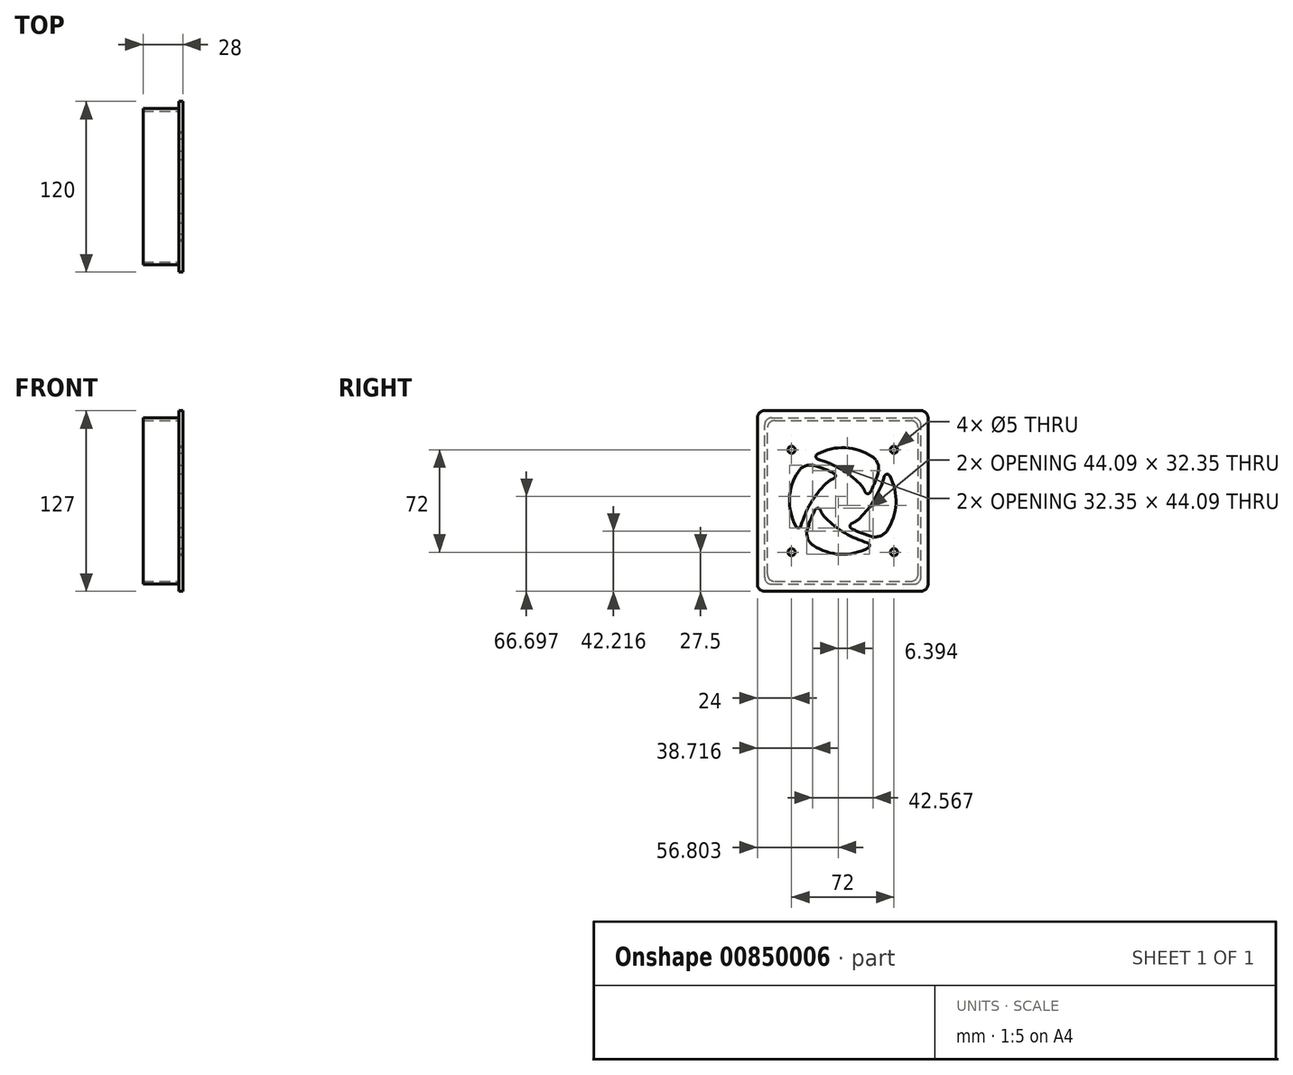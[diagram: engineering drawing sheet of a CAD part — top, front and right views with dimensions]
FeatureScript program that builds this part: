
annotation { "Feature Type Name" : "Feature", "Feature Type Description" : "" }
export const myFeature = defineFeature(function(context is Context, id is Id, definition is map)
    precondition{}
    {
        {
            var Q0;
            Q0=qCreatedBy(makeId("Right.planeOp"),FACE);
            var sketch = newSketch(context, id + "F0", { "sketchPlane" : qUnion([Q0])});
            skLineSegment(sketch, "E0.bottom", {"start": v(60, 63.5) * mm, "end": v(-60, 63.5) * mm});
            skLineSegment(sketch, "E0.top", {"start": v(60, -63.5) * mm, "end": v(-60, -63.5) * mm});
            skLineSegment(sketch, "E0.left", {"start": v(60, 63.5) * mm, "end": v(60, -63.5) * mm});
            skLineSegment(sketch, "E0.right", {"start": v(-60, 63.5) * mm, "end": v(-60, -63.5) * mm});
            skPoint(sketch, "E0.middle", {"position": v(0, 0) * mm});
            skSolve(sketch);
        }
        {
            var Q0;
            Q0 = qSketchRegion(id + "F0", true);
            extrude(context, id + "F1", {"entities" : qUnion([Q0]), "depth" : 3 * mm, "offsetDistance" : 25 * mm});
        }
        {
            var Q0;
            Q0=makeQuery(id+"F1.opExtrude","SWEPT_EDGE",EDGE,{"disambiguationData":[OSD([sQuery(id+"F0.wireOp",EDGE,"E0.bottom"),sQuery(id+"F0.wireOp",EDGE,"E0.right")])]});
            var Q1;
            Q1=makeQuery(id+"F1.opExtrude","SWEPT_EDGE",EDGE,{"disambiguationData":[OSD([sQuery(id+"F0.wireOp",EDGE,"E0.bottom"),sQuery(id+"F0.wireOp",EDGE,"E0.left")])]});
            var Q2;
            Q2=makeQuery(id+"F1.opExtrude","SWEPT_EDGE",EDGE,{"disambiguationData":[OSD([sQuery(id+"F0.wireOp",EDGE,"E0.top"),sQuery(id+"F0.wireOp",EDGE,"E0.left")])]});
            var Q3;
            Q3=makeQuery(id+"F1.opExtrude","SWEPT_EDGE",EDGE,{"disambiguationData":[OSD([sQuery(id+"F0.wireOp",EDGE,"E0.top"),sQuery(id+"F0.wireOp",EDGE,"E0.right")])]});
            fillet(context, id + "F2", {"entities" : qUnion([Q0, Q1, Q2, Q3]), "radius" : 5 * mm, "tangentPropagation" : true, "allowEdgeOverflow" : false});
        }
        {
            var Q0;
            Q0=makeQuery(id+"F1.opExtrude","CAP_FACE",FACE,{"disambiguationData":[OSD([sQuery(id+"F0.wireOp",EDGE,"E0.bottom"),sQuery(id+"F0.wireOp",EDGE,"E0.top"),sQuery(id+"F0.wireOp",EDGE,"E0.left"),sQuery(id+"F0.wireOp",EDGE,"E0.right")])],"isStart":true});
            var sketch = newSketch(context, id + "F3", { "sketchPlane" : qUnion([Q0])});
            skLineSegment(sketch, "E1.bottom", {"start": v(50, -58.5) * mm, "end": v(-50, -58.5) * mm});
            skLineSegment(sketch, "E1.top", {"start": v(50, 58.5) * mm, "end": v(-50, 58.5) * mm});
            skLineSegment(sketch, "E1.left", {"start": v(55, -53.5) * mm, "end": v(55, 53.5) * mm});
            skLineSegment(sketch, "E1.right", {"start": v(-55, -53.5) * mm, "end": v(-55, 53.5) * mm});
            skPoint(sketch, "E1.middle", {"position": v(0, 0) * mm});
            skLineSegment(sketch, "E2.0", {"start": v(53, -51.5) * mm, "end": v(53, 51.5) * mm});
            skLineSegment(sketch, "E2.1", {"start": v(48, -56.5) * mm, "end": v(-48, -56.5) * mm});
            skLineSegment(sketch, "E2.2", {"start": v(-53, -51.5) * mm, "end": v(-53, 51.5) * mm});
            skLineSegment(sketch, "E2.3", {"start": v(48, 56.5) * mm, "end": v(-48, 56.5) * mm});
            skPoint(sketch, "E3.visualSharp", {"position": v(53, 56.5) * mm});
            skArc(sketch, "E3.filletArc", {"start": v(53, 51.5) * mm, "mid": v(51.54, 55.04) * mm, "end": v(48, 56.5) * mm});
            skPoint(sketch, "E4.visualSharp", {"position": v(55, 58.5) * mm});
            skArc(sketch, "E4.filletArc", {"start": v(55, 53.5) * mm, "mid": v(53.54, 57.04) * mm, "end": v(50, 58.5) * mm});
            skPoint(sketch, "E5.visualSharp", {"position": v(53, -56.5) * mm});
            skArc(sketch, "E5.filletArc", {"start": v(48, -56.5) * mm, "mid": v(51.54, -55.04) * mm, "end": v(53, -51.5) * mm});
            skPoint(sketch, "E6.visualSharp", {"position": v(55, -58.5) * mm});
            skArc(sketch, "E6.filletArc", {"start": v(50, -58.5) * mm, "mid": v(53.54, -57.04) * mm, "end": v(55, -53.5) * mm});
            skPoint(sketch, "E7.visualSharp", {"position": v(-53, 56.5) * mm});
            skArc(sketch, "E7.filletArc", {"start": v(-48, 56.5) * mm, "mid": v(-51.54, 55.04) * mm, "end": v(-53, 51.5) * mm});
            skPoint(sketch, "E8.visualSharp", {"position": v(-55, 58.5) * mm});
            skArc(sketch, "E8.filletArc", {"start": v(-50, 58.5) * mm, "mid": v(-53.54, 57.04) * mm, "end": v(-55, 53.5) * mm});
            skPoint(sketch, "E9.visualSharp", {"position": v(-53, -56.5) * mm});
            skArc(sketch, "E9.filletArc", {"start": v(-53, -51.5) * mm, "mid": v(-51.54, -55.04) * mm, "end": v(-48, -56.5) * mm});
            skPoint(sketch, "E10.visualSharp", {"position": v(-55, -58.5) * mm});
            skArc(sketch, "E10.filletArc", {"start": v(-55, -53.5) * mm, "mid": v(-53.54, -57.04) * mm, "end": v(-50, -58.5) * mm});
            skSolve(sketch);
        }
        {
            var Q0;
            Q0 = qSketchRegion(id + "F3", true);
            extrude(context, id + "F4", {"entities" : qUnion([Q0]), "operationType" : NewBodyOperationType.ADD, "depth" : 25 * mm, "offsetDistance" : 25 * mm});
        }
        {
            var Q0;
            Q0=makeQuery(id+"F4.boolean.opBoolean","SPLIT",FACE,{"disambiguationData":[TD([makeQuery(id+"F4.opExtrude","SWEPT_FACE",FACE,{"disambiguationData":[OSD([sQuery(id+"F3.wireOp",EDGE,"E2.0")])]})])],"derivedFrom":makeQuery(id+"F1.opExtrude","CAP_FACE",FACE,{"disambiguationData":[OSD([sQuery(id+"F0.wireOp",EDGE,"E0.bottom"),sQuery(id+"F0.wireOp",EDGE,"E0.top"),sQuery(id+"F0.wireOp",EDGE,"E0.left"),sQuery(id+"F0.wireOp",EDGE,"E0.right")])],"isStart":true})});
            var sketch = newSketch(context, id + "F5", { "sketchPlane" : qUnion([Q0])});
            skCircle(sketch, "E11", {"center": v(36, 36) * mm, "radius": 2.5 * mm});
            skCircle(sketch, "E12.0.1.0", {"center": v(36, -36) * mm, "radius": 2.5 * mm});
            skCircle(sketch, "E12.1.0.0", {"center": v(-36, 36) * mm, "radius": 2.5 * mm});
            skCircle(sketch, "E12.1.1.0", {"center": v(-36, -36) * mm, "radius": 2.5 * mm});
            skCircle(sketch, "E12.2.0.0", {"center": v(-108, 36) * mm, "radius": 2.5 * mm});
            skCircle(sketch, "E12.2.1.0", {"center": v(-108, -36) * mm, "radius": 2.5 * mm});
            skLineSegment(sketch, "E12.direction1", {"start": v(36, 36) * mm, "end": v(-36, 36) * mm, "construction": true});
            skLineSegment(sketch, "E12.direction2", {"start": v(36, 36) * mm, "end": v(36, -36) * mm, "construction": true});
            skSolve(sketch);
        }
        {
            var Q0;
            Q0 = qSketchRegion(id + "F5", true);
            extrude(context, id + "F6", {"entities" : qUnion([Q0]), "operationType" : NewBodyOperationType.REMOVE, "endBound" : BoundingType.THROUGH_ALL, "oppositeDirection" : true, "depth" : 25 * mm, "offsetDistance" : 25 * mm});
        }
        {
            var Q0;
            Q0=makeQuery(id+"F4.boolean.opBoolean","SPLIT",FACE,{"disambiguationData":[TD([makeQuery(id+"F4.opExtrude","SWEPT_FACE",FACE,{"disambiguationData":[OSD([sQuery(id+"F3.wireOp",EDGE,"E2.0")])]})])],"derivedFrom":makeQuery(id+"F1.opExtrude","CAP_FACE",FACE,{"disambiguationData":[OSD([sQuery(id+"F0.wireOp",EDGE,"E0.bottom"),sQuery(id+"F0.wireOp",EDGE,"E0.top"),sQuery(id+"F0.wireOp",EDGE,"E0.left"),sQuery(id+"F0.wireOp",EDGE,"E0.right")])],"isStart":true})});
            var sketch = newSketch(context, id + "F7", { "sketchPlane" : qUnion([Q0])});
            skArc(sketch, "E13", {"start": v(12.02, 12.02) * mm, "mid": v(7.39, 15.3) * mm, "end": v(1.93, 16.89) * mm});
            skArc(sketch, "E14", {"start": v(30.43, -21.9) * mm, "mid": v(37.4, 2.83) * mm, "end": v(26.8, 26.23) * mm});
            skArc(sketch, "E15", {"start": v(30.43, -21.9) * mm, "mid": v(23.69, -3.6) * mm, "end": v(12.02, 12.02) * mm});
            skArc(sketch, "E16.0", {"start": v(26.23, -26.8) * mm, "mid": v(22.89, -13.87) * mm, "end": v(16.89, -1.93) * mm});
            skArc(sketch, "E17", {"start": v(-21.9, -30.43) * mm, "mid": v(-3.6, -23.69) * mm, "end": v(12.02, -12.02) * mm});
            skArc(sketch, "E18.0", {"start": v(-26.8, -26.23) * mm, "mid": v(-13.87, -22.89) * mm, "end": v(-1.93, -16.89) * mm});
            skArc(sketch, "E19.trimOffspring", {"start": v(-21.9, -30.43) * mm, "mid": v(2.83, -37.4) * mm, "end": v(26.23, -26.8) * mm});
            skArc(sketch, "E20.trimOffspring", {"start": v(12.02, -12.02) * mm, "mid": v(15.3, -7.39) * mm, "end": v(16.89, -1.93) * mm});
            skArc(sketch, "E21", {"start": v(-30.43, 21.9) * mm, "mid": v(-23.69, 3.6) * mm, "end": v(-12.02, -12.02) * mm});
            skArc(sketch, "E22.0", {"start": v(-26.23, 26.8) * mm, "mid": v(-22.89, 13.87) * mm, "end": v(-16.89, 1.93) * mm});
            skArc(sketch, "E23.trimOffspring", {"start": v(-12.02, -12.02) * mm, "mid": v(-7.39, -15.3) * mm, "end": v(-1.93, -16.89) * mm});
            skArc(sketch, "E24.trimOffspring", {"start": v(-30.43, 21.9) * mm, "mid": v(-37.4, -2.83) * mm, "end": v(-26.8, -26.23) * mm});
            skArc(sketch, "E25.0", {"start": v(26.8, 26.23) * mm, "mid": v(13.87, 22.89) * mm, "end": v(1.93, 16.89) * mm});
            skArc(sketch, "E26.trimOffspring", {"start": v(-12.02, 12.02) * mm, "mid": v(-15.3, 7.39) * mm, "end": v(-16.89, 1.93) * mm});
            skArc(sketch, "E27.trimOffspring", {"start": v(21.9, 30.43) * mm, "mid": v(3.6, 23.69) * mm, "end": v(-12.02, 12.02) * mm});
            skArc(sketch, "E28.trimOffspring", {"start": v(21.9, 30.43) * mm, "mid": v(-2.83, 37.4) * mm, "end": v(-26.23, 26.8) * mm});
            skSolve(sketch);
        }
        {
            var Q0;
            Q0=makeQuery(id+"F7.imprint","IMPRINT",FACE,{"disambiguationData":[TD([[makeQuery(id+"F7.imprint","IMPRINT",EDGE,{"derivedFrom":sQuery(id+"F7.wireOp",EDGE,"E16.0")}),1.0]])]});
            extrude(context, id + "F8", {"entities" : qUnion([Q0]), "operationType" : NewBodyOperationType.REMOVE, "endBound" : BoundingType.THROUGH_ALL, "oppositeDirection" : true, "depth" : 25 * mm, "offsetDistance" : 25 * mm});
        }
        {
            var Q0;
            Q0=makeQuery(id+"F7.imprint","IMPRINT",FACE,{"disambiguationData":[TD([[makeQuery(id+"F7.imprint","IMPRINT",EDGE,{"derivedFrom":sQuery(id+"F7.wireOp",EDGE,"E13")}),-1.0]])]});
            var Q1;
            Q1=makeQuery(id+"F7.imprint","IMPRINT",FACE,{"disambiguationData":[TD([[makeQuery(id+"F7.imprint","IMPRINT",EDGE,{"derivedFrom":sQuery(id+"F7.wireOp",EDGE,"E16.0")}),1.0]])]});
            var Q2;
            Q2=makeQuery(id+"F7.imprint","IMPRINT",FACE,{"disambiguationData":[TD([[makeQuery(id+"F7.imprint","IMPRINT",EDGE,{"derivedFrom":sQuery(id+"F7.wireOp",EDGE,"E18.0")}),1.0]])]});
            var Q3;
            Q3=makeQuery(id+"F7.imprint","IMPRINT",FACE,{"disambiguationData":[TD([[makeQuery(id+"F7.imprint","IMPRINT",EDGE,{"derivedFrom":sQuery(id+"F7.wireOp",EDGE,"E22.0")}),1.0]])]});
            extrude(context, id + "F9", {"entities" : qUnion([Q0, Q1, Q2, Q3]), "operationType" : NewBodyOperationType.REMOVE, "endBound" : BoundingType.THROUGH_ALL, "oppositeDirection" : true, "depth" : 25 * mm, "offsetDistance" : 25 * mm});
        }
        {
            var Q0;
            Q0=makeQuery(id+"F8.boolean.opBoolean","COPY",EDGE,{"derivedFrom":makeQuery(id+"F8.opExtrude","SWEPT_EDGE",EDGE,{"disambiguationData":[OSD([sQuery(id+"F7.wireOp",EDGE,"E16.0"),sQuery(id+"F7.wireOp",EDGE,"E19.trimOffspring")])]})});
            var Q1;
            Q1=makeQuery(id+"F9.boolean.opBoolean","COPY",EDGE,{"derivedFrom":makeQuery(id+"F9.opExtrude","SWEPT_EDGE",EDGE,{"disambiguationData":[OSD([sQuery(id+"F7.wireOp",EDGE,"E14"),sQuery(id+"F7.wireOp",EDGE,"E25.0")])]})});
            var Q2;
            Q2=makeQuery(id+"F9.boolean.opBoolean","COPY",EDGE,{"derivedFrom":makeQuery(id+"F9.opExtrude","SWEPT_EDGE",EDGE,{"disambiguationData":[OSD([sQuery(id+"F7.wireOp",EDGE,"E18.0"),sQuery(id+"F7.wireOp",EDGE,"E24.trimOffspring")])]})});
            var Q3;
            Q3=makeQuery(id+"F9.boolean.opBoolean","COPY",EDGE,{"derivedFrom":makeQuery(id+"F9.opExtrude","SWEPT_EDGE",EDGE,{"disambiguationData":[OSD([sQuery(id+"F7.wireOp",EDGE,"E22.0"),sQuery(id+"F7.wireOp",EDGE,"E28.trimOffspring")])]})});
            fillet(context, id + "F10", {"entities" : qUnion([Q0, Q1, Q2, Q3]), "radius" : 10 * mm, "tangentPropagation" : true, "allowEdgeOverflow" : false});
        }
        {
            var Q0;
            Q0=makeQuery(id+"F9.boolean.opBoolean","COPY",EDGE,{"derivedFrom":makeQuery(id+"F9.opExtrude","SWEPT_EDGE",EDGE,{"disambiguationData":[OSD([sQuery(id+"F7.wireOp",EDGE,"E27.trimOffspring"),sQuery(id+"F7.wireOp",EDGE,"E28.trimOffspring")])]})});
            var Q1;
            Q1=makeQuery(id+"F9.boolean.opBoolean","COPY",EDGE,{"derivedFrom":makeQuery(id+"F9.opExtrude","SWEPT_EDGE",EDGE,{"disambiguationData":[OSD([sQuery(id+"F7.wireOp",EDGE,"E13"),sQuery(id+"F7.wireOp",EDGE,"E25.0")])]})});
            var Q2;
            Q2=makeQuery(id+"F9.boolean.opBoolean","COPY",EDGE,{"derivedFrom":makeQuery(id+"F9.opExtrude","SWEPT_EDGE",EDGE,{"disambiguationData":[OSD([sQuery(id+"F7.wireOp",EDGE,"E14"),sQuery(id+"F7.wireOp",EDGE,"E15")])]})});
            var Q3;
            Q3=makeQuery(id+"F8.boolean.opBoolean","COPY",EDGE,{"derivedFrom":makeQuery(id+"F8.opExtrude","SWEPT_EDGE",EDGE,{"disambiguationData":[OSD([sQuery(id+"F7.wireOp",EDGE,"E16.0"),sQuery(id+"F7.wireOp",EDGE,"E20.trimOffspring")])]})});
            var Q4;
            Q4=makeQuery(id+"F8.boolean.opBoolean","COPY",EDGE,{"derivedFrom":makeQuery(id+"F8.opExtrude","SWEPT_EDGE",EDGE,{"disambiguationData":[OSD([sQuery(id+"F7.wireOp",EDGE,"E17"),sQuery(id+"F7.wireOp",EDGE,"E19.trimOffspring")])]})});
            var Q5;
            Q5=makeQuery(id+"F9.boolean.opBoolean","COPY",EDGE,{"derivedFrom":makeQuery(id+"F9.opExtrude","SWEPT_EDGE",EDGE,{"disambiguationData":[OSD([sQuery(id+"F7.wireOp",EDGE,"E18.0"),sQuery(id+"F7.wireOp",EDGE,"E23.trimOffspring")])]})});
            var Q6;
            Q6=makeQuery(id+"F9.boolean.opBoolean","COPY",EDGE,{"derivedFrom":makeQuery(id+"F9.opExtrude","SWEPT_EDGE",EDGE,{"disambiguationData":[OSD([sQuery(id+"F7.wireOp",EDGE,"E21"),sQuery(id+"F7.wireOp",EDGE,"E24.trimOffspring")])]})});
            var Q7;
            Q7=makeQuery(id+"F9.boolean.opBoolean","COPY",EDGE,{"derivedFrom":makeQuery(id+"F9.opExtrude","SWEPT_EDGE",EDGE,{"disambiguationData":[OSD([sQuery(id+"F7.wireOp",EDGE,"E22.0"),sQuery(id+"F7.wireOp",EDGE,"E26.trimOffspring")])]})});
            fillet(context, id + "F11", {"entities" : qUnion([Q0, Q1, Q2, Q3, Q4, Q5, Q6, Q7]), "radius" : 2 * mm, "tangentPropagation" : true, "allowEdgeOverflow" : false});
        }
    });
